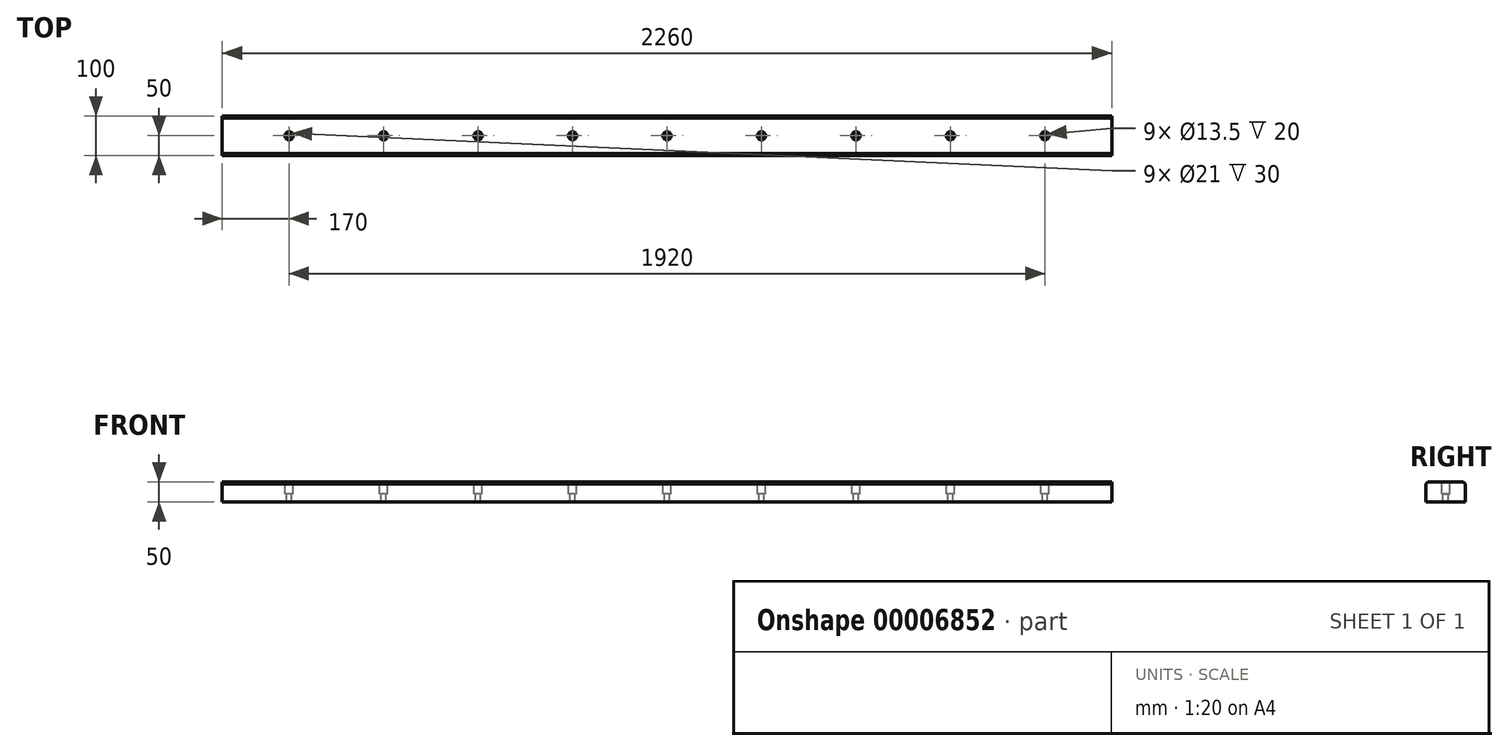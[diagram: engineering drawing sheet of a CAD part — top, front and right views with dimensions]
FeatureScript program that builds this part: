
annotation { "Feature Type Name" : "Feature", "Feature Type Description" : "" }
export const myFeature = defineFeature(function(context is Context, id is Id, definition is map)
    precondition{}
    {
        {
            var Q0;
            Q0=qCreatedBy(makeId("Right.planeOp"),FACE);
            var sketch = newSketch(context, id + "F0", { "sketchPlane" : qUnion([Q0])});
            skLineSegment(sketch, "E0.rect.bottom", {"start": v(-50, 25) * mm, "end": v(50, 25) * mm});
            skLineSegment(sketch, "E0.rect.top", {"start": v(-50, -25) * mm, "end": v(50, -25) * mm});
            skLineSegment(sketch, "E0.rect.left", {"start": v(-50, 25) * mm, "end": v(-50, -25) * mm});
            skLineSegment(sketch, "E0.rect.right", {"start": v(50, 25) * mm, "end": v(50, -25) * mm});
            skPoint(sketch, "E0.rect.middle", {"position": v(0, 0) * mm});
            skSolve(sketch);
        }
        {
            var Q0;
            Q0 = qSketchRegion(id + "F0", true);
            extrude(context, id + "F1", {"entities" : qUnion([Q0]), "endBound" : BoundingType.SYMMETRIC, "depth" : 2260 * mm});
        }
        {
            var Q0;
            Q0=makeQuery(id+"F1.opExtrude","SWEPT_FACE",FACE,{"disambiguationData":[OSD([sQuery(id+"F0.wireOp",EDGE,"E0.rect.bottom")])]});
            var sketch = newSketch(context, id + "F2", { "sketchPlane" : qUnion([Q0])});
            skLineSegment(sketch, "E1", {"start": v(0, -50) * mm, "end": v(0, 50) * mm, "construction": true});
            skCircle(sketch, "E2", {"center": v(0, 0) * mm, "radius": 6.75 * mm});
            skCircle(sketch, "E3.1.0.0", {"center": v(240, 0) * mm, "radius": 6.75 * mm});
            skCircle(sketch, "E3.2.0.0", {"center": v(480, 0) * mm, "radius": 6.75 * mm});
            skCircle(sketch, "E3.3.0.0", {"center": v(720, 0) * mm, "radius": 6.75 * mm});
            skCircle(sketch, "E3.4.0.0", {"center": v(960, 0) * mm, "radius": 6.75 * mm});
            skLineSegment(sketch, "E3.direction1", {"start": v(0, 0) * mm, "end": v(240, 0) * mm, "construction": true});
            skCircle(sketch, "E4.0.MirrorC", {"center": v(-960, 0) * mm, "radius": 6.75 * mm});
            skCircle(sketch, "E4.1.MirrorC", {"center": v(-720, 0) * mm, "radius": 6.75 * mm});
            skCircle(sketch, "E4.2.MirrorC", {"center": v(-480, 0) * mm, "radius": 6.75 * mm});
            skCircle(sketch, "E4.3.MirrorC", {"center": v(-240, 0) * mm, "radius": 6.75 * mm});
            skSolve(sketch);
        }
        {
            var Q0;
            Q0 = qSketchRegion(id + "F2", true);
            extrude(context, id + "F3", {"entities" : qUnion([Q0]), "operationType" : NewBodyOperationType.REMOVE, "endBound" : BoundingType.THROUGH_ALL, "oppositeDirection" : true, "depth" : 25 * mm});
        }
        {
            var Q0;
            Q0=makeQuery(id+"F1.opExtrude","SWEPT_FACE",FACE,{"disambiguationData":[OSD([sQuery(id+"F0.wireOp",EDGE,"E0.rect.bottom")])]});
            var sketch = newSketch(context, id + "F4", { "sketchPlane" : qUnion([Q0])});
            skCircle(sketch, "E5", {"center": v(-960, 0) * mm, "radius": 10.5 * mm});
            skCircle(sketch, "E6.1.0.0", {"center": v(-720, 0) * mm, "radius": 10.5 * mm});
            skCircle(sketch, "E6.2.0.0", {"center": v(-480, 0) * mm, "radius": 10.5 * mm});
            skCircle(sketch, "E6.3.0.0", {"center": v(-240, 0) * mm, "radius": 10.5 * mm});
            skCircle(sketch, "E6.4.0.0", {"center": v(0, 0) * mm, "radius": 10.5 * mm});
            skCircle(sketch, "E6.5.0.0", {"center": v(240, 0) * mm, "radius": 10.5 * mm});
            skCircle(sketch, "E6.6.0.0", {"center": v(480, 0) * mm, "radius": 10.5 * mm});
            skCircle(sketch, "E6.7.0.0", {"center": v(720, 0) * mm, "radius": 10.5 * mm});
            skCircle(sketch, "E6.8.0.0", {"center": v(960, 0) * mm, "radius": 10.5 * mm});
            skLineSegment(sketch, "E6.direction1", {"start": v(-960, 0) * mm, "end": v(-720, 0) * mm, "construction": true});
            skSolve(sketch);
        }
        {
            var Q0;
            Q0 = qSketchRegion(id + "F4", true);
            extrude(context, id + "F5", {"entities" : qUnion([Q0]), "operationType" : NewBodyOperationType.REMOVE, "oppositeDirection" : true, "depth" : 30 * mm});
        }
        {
            var Q0;
            Q0=makeQuery(id+"F1.opExtrude","SWEPT_EDGE",EDGE,{"disambiguationData":[OSD([sQuery(id+"F0.wireOp",EDGE,"E0.rect.bottom"),sQuery(id+"F0.wireOp",EDGE,"E0.rect.right")])]});
            var Q1;
            Q1=makeQuery(id+"F1.opExtrude","SWEPT_EDGE",EDGE,{"disambiguationData":[OSD([sQuery(id+"F0.wireOp",EDGE,"E0.rect.bottom"),sQuery(id+"F0.wireOp",EDGE,"E0.rect.left")])]});
            chamfer(context, id + "F6", {"entities" : qUnion([Q0, Q1]), "width" : 5 * mm, "tangentPropagation" : true});
        }
    });
